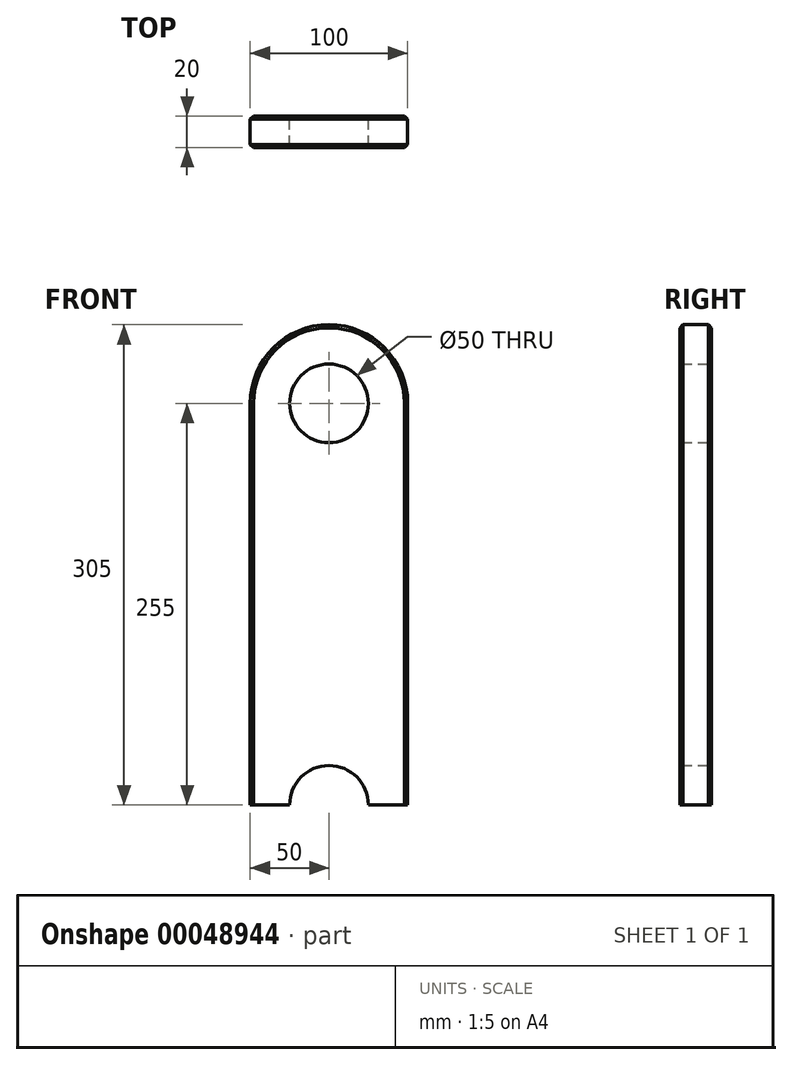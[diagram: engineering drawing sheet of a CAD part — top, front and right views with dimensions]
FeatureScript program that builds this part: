
annotation { "Feature Type Name" : "Feature", "Feature Type Description" : "" }
export const myFeature = defineFeature(function(context is Context, id is Id, definition is map)
    precondition{}
    {
        {
            var Q0;
            Q0=qCreatedBy(makeId("Front.planeOp"),FACE);
            var sketch = newSketch(context, id + "F0", { "sketchPlane" : qUnion([Q0])});
            skLineSegment(sketch, "E0.rect.bottom", {"start": v(50, 127.5) * mm, "end": v(-50, 127.5) * mm});
            skLineSegment(sketch, "E0.rect.top", {"start": v(50, -127.5) * mm, "end": v(-50, -127.5) * mm});
            skLineSegment(sketch, "E0.rect.left", {"start": v(50, 127.5) * mm, "end": v(50, -127.5) * mm});
            skLineSegment(sketch, "E0.rect.right", {"start": v(-50, 127.5) * mm, "end": v(-50, -127.5) * mm});
            skPoint(sketch, "E0.rect.middle", {"position": v(0, 0) * mm});
            skArc(sketch, "E1", {"start": v(50, 127.5) * mm, "mid": v(0, 177.5) * mm, "end": v(-50, 127.5) * mm});
            skArc(sketch, "E2", {"start": v(50, -127.5) * mm, "mid": v(0, -177.5) * mm, "end": v(-50, -127.5) * mm});
            skCircle(sketch, "E3", {"center": v(0, 127.5) * mm, "radius": 25 * mm});
            skCircle(sketch, "E4", {"center": v(0, -127.5) * mm, "radius": 25 * mm});
            skSolve(sketch);
        }
        {
            var Q0;
            {var subQ4=sQuery(id+"F0.wireOp",EDGE,"E1");Q0=makeQuery(id+"F0.imprint","IMPRINT",FACE,{"disambiguationData":[TD([[makeQuery(id+"F0.imprint","IMPRINT",EDGE,{"derivedFrom":subQ4}),1.0]])]});}
            var Q1;
            {var subQ4=sQuery(id+"F0.wireOp",EDGE,"E2");Q1=makeQuery(id+"F0.imprint","IMPRINT",FACE,{"disambiguationData":[TD([[makeQuery(id+"F0.imprint","IMPRINT",EDGE,{"derivedFrom":subQ4}),-1.0]])]});}
            var Q2;
            {var subQ5=sQuery(id+"F0.wireOp",EDGE,"E0.rect.left");Q2=makeQuery(id+"F0.imprint","IMPRINT",FACE,{"disambiguationData":[TD([[makeQuery(id+"F0.imprint","IMPRINT",EDGE,{"derivedFrom":subQ5}),-1.0]])]});}
            extrude(context, id + "F1", {"entities" : qUnion([Q0, Q1, Q2]), "depth" : 20 * mm});
        }
        {
            var Q0;
            Q0=makeQuery(id+"F1.opExtrude","CAP_EDGE",EDGE,{"disambiguationData":[OSD([sQuery(id+"F0.wireOp",EDGE,"E2")])],"isStart":true});
            var Q1;
            Q1=makeQuery(id+"F1.opExtrude","CAP_EDGE",EDGE,{"disambiguationData":[OSD([sQuery(id+"F0.wireOp",EDGE,"E0.rect.right")])],"isStart":true});
            var Q2;
            Q2=makeQuery(id+"F1.opExtrude","CAP_EDGE",EDGE,{"disambiguationData":[OSD([sQuery(id+"F0.wireOp",EDGE,"E1")])],"isStart":true});
            var Q3;
            Q3=makeQuery(id+"F1.opExtrude","CAP_EDGE",EDGE,{"disambiguationData":[OSD([sQuery(id+"F0.wireOp",EDGE,"E0.rect.left")])],"isStart":true});
            var Q4;
            Q4=makeQuery(id+"F1.opExtrude","CAP_EDGE",EDGE,{"disambiguationData":[OSD([sQuery(id+"F0.wireOp",EDGE,"E0.rect.left")])],"isStart":false});
            var Q5;
            Q5=makeQuery(id+"F1.opExtrude","CAP_EDGE",EDGE,{"disambiguationData":[OSD([sQuery(id+"F0.wireOp",EDGE,"E2")])],"isStart":false});
            var Q6;
            Q6=makeQuery(id+"F1.opExtrude","CAP_EDGE",EDGE,{"disambiguationData":[OSD([sQuery(id+"F0.wireOp",EDGE,"E0.rect.right")])],"isStart":false});
            var Q7;
            Q7=makeQuery(id+"F1.opExtrude","CAP_EDGE",EDGE,{"disambiguationData":[OSD([sQuery(id+"F0.wireOp",EDGE,"E1")])],"isStart":false});
            chamfer(context, id + "F2", {"entities" : qUnion([Q0, Q1, Q2, Q3, Q4, Q5, Q6, Q7]), "chamferType" : ChamferType.OFFSET_ANGLE, "width" : 2 * mm, "oppositeDirection" : false, "angle" : 45 * degree, "tangentPropagation" : true});
        }
    });
